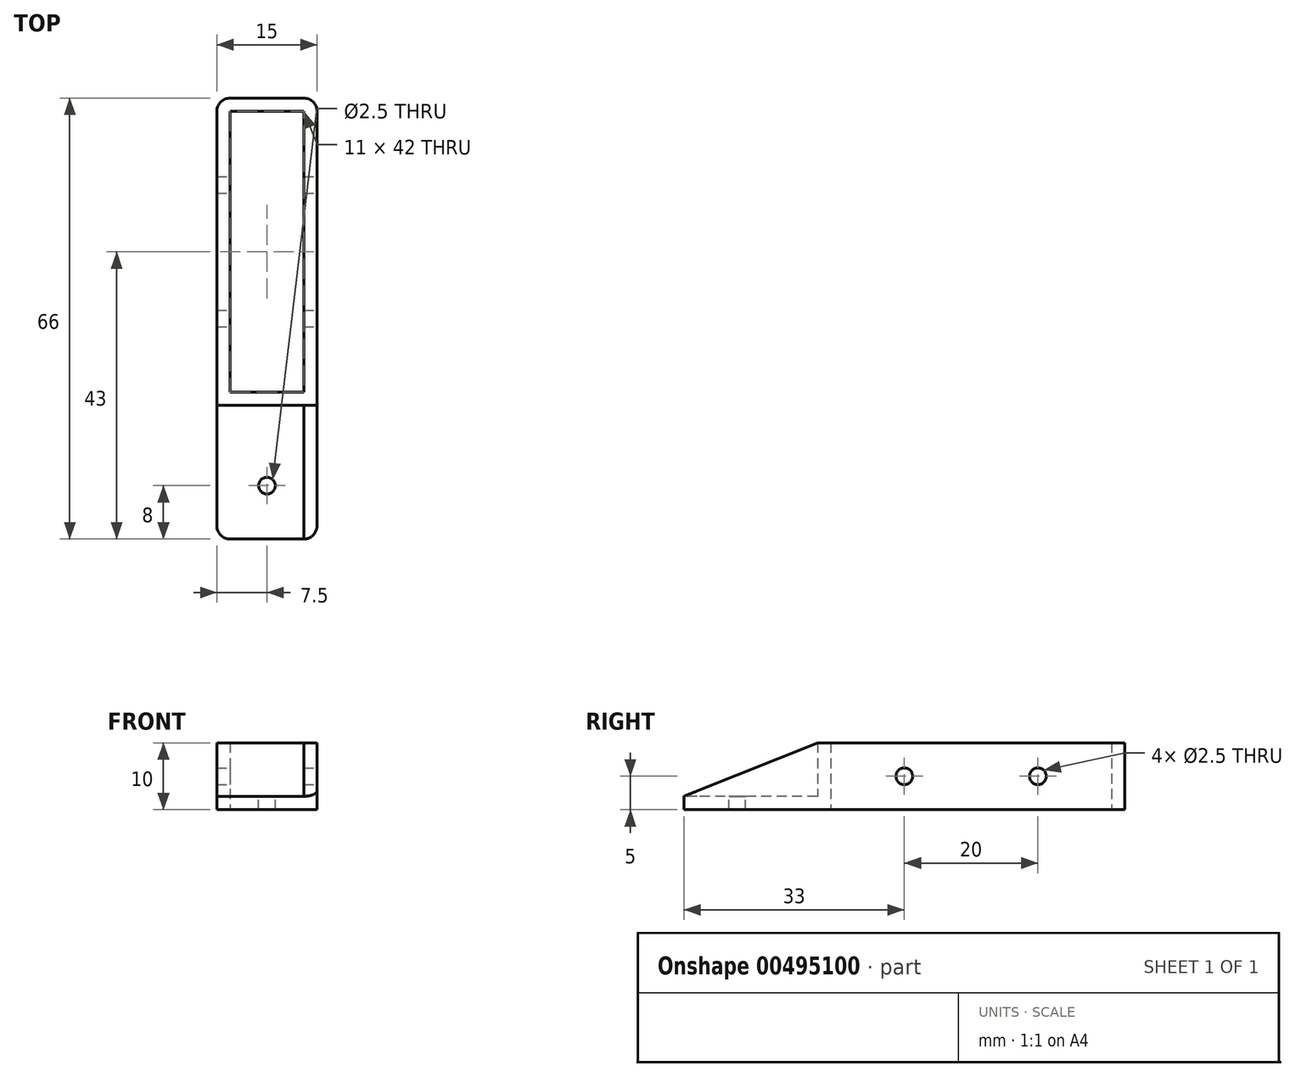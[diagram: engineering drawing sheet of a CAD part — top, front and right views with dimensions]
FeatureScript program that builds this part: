
annotation { "Feature Type Name" : "Feature", "Feature Type Description" : "" }
export const myFeature = defineFeature(function(context is Context, id is Id, definition is map)
    precondition{}
    {
        {
            var Q0;
            Q0=qCreatedBy(makeId("Top.planeOp"),FACE);
            var sketch = newSketch(context, id + "F0", { "sketchPlane" : qUnion([Q0])});
            skLineSegment(sketch, "E0.bottom", {"start": v(0, 0) * mm, "end": v(11, 0) * mm});
            skLineSegment(sketch, "E0.top", {"start": v(0, 42) * mm, "end": v(11, 42) * mm});
            skLineSegment(sketch, "E0.left", {"start": v(0, 0) * mm, "end": v(0, 42) * mm});
            skLineSegment(sketch, "E0.right", {"start": v(11, 0) * mm, "end": v(11, 42) * mm});
            skSolve(sketch);
        }
        {
            var Q0;
            Q0 = qSketchRegion(id + "F0", true);
            extrude(context, id + "F1", {"entities" : qUnion([Q0]), "depth" : 10 * mm});
        }
        {
            var Q0;
            Q0=makeQuery(id+"F1.opExtrude","CAP_FACE",FACE,{"disambiguationData":[OSD([sQuery(id+"F0.wireOp",EDGE,"E0.bottom"),sQuery(id+"F0.wireOp",EDGE,"E0.top"),sQuery(id+"F0.wireOp",EDGE,"E0.left"),sQuery(id+"F0.wireOp",EDGE,"E0.right")])],"isStart":false});
            var Q1;
            Q1=makeQuery(id+"F1.opExtrude","CAP_FACE",FACE,{"disambiguationData":[OSD([sQuery(id+"F0.wireOp",EDGE,"E0.bottom"),sQuery(id+"F0.wireOp",EDGE,"E0.top"),sQuery(id+"F0.wireOp",EDGE,"E0.left"),sQuery(id+"F0.wireOp",EDGE,"E0.right")])],"isStart":true});
            shell(context, id + "F2", {"entities" : qUnion([Q0, Q1]), "thickness" : 2 * mm, "oppositeDirection" : true});
        }
        {
            var Q0;
            Q0=qCreatedBy(makeId("Top.planeOp"),FACE);
            var sketch = newSketch(context, id + "F3", { "sketchPlane" : qUnion([Q0])});
            skLineSegment(sketch, "E1", {"start": v(-7.9, -2) * mm, "end": v(18.9, -2) * mm, "construction": true});
            skLineSegment(sketch, "E2", {"start": v(-2, 1.2) * mm, "end": v(-2, -8.45) * mm, "construction": true});
            skLineSegment(sketch, "E3", {"start": v(13, -0.65) * mm, "end": v(13, -7.97) * mm, "construction": true});
            skLineSegment(sketch, "E4.bottom", {"start": v(-2, -2) * mm, "end": v(13, -2) * mm});
            skLineSegment(sketch, "E4.top", {"start": v(-2, -22) * mm, "end": v(13, -22) * mm});
            skLineSegment(sketch, "E4.left", {"start": v(-2, -2) * mm, "end": v(-2, -22) * mm});
            skLineSegment(sketch, "E4.right", {"start": v(13, -2) * mm, "end": v(13, -22) * mm});
            skSolve(sketch);
        }
        {
            var Q0;
            Q0 = qSketchRegion(id + "F3", true);
            extrude(context, id + "F4", {"entities" : qUnion([Q0]), "operationType" : NewBodyOperationType.ADD, "depth" : 2 * mm});
        }
        {
            var Q0;
            Q0=makeQuery(id+"F4.boolean.opBoolean","MERGE",FACE,{"derivedFrom":[makeQuery(id+"F1.opExtrude","SWEPT_FACE",FACE,{"disambiguationData":[OSD([sQuery(id+"F0.wireOp",EDGE,"E0.right")])]}),makeQuery(id+"F4.opExtrude","SWEPT_FACE",FACE,{"disambiguationData":[OSD([sQuery(id+"F3.wireOp",EDGE,"E4.right")])]})]});
            var sketch = newSketch(context, id + "F5", { "sketchPlane" : qUnion([Q0])});
            skLineSegment(sketch, "E5", {"start": v(-22, 2) * mm, "end": v(-2, 10) * mm});
            skLineSegment(sketch, "E6", {"start": v(-22, 2) * mm, "end": v(-2, 2) * mm});
            skLineSegment(sketch, "E7", {"start": v(-2, 2) * mm, "end": v(-2, 10) * mm});
            skSolve(sketch);
        }
        {
            var Q0;
            Q0 = qSketchRegion(id + "F5", true);
            extrude(context, id + "F6", {"entities" : qUnion([Q0]), "operationType" : NewBodyOperationType.ADD, "oppositeDirection" : true, "depth" : 2 * mm});
        }
        {
            var Q0;
            Q0=qCreatedBy(makeId("Right.planeOp"),FACE);
            cPlane(context, id + "F7", {"entities" : qUnion([Q0]), "cplaneType" : CPlaneType.OFFSET, "offset" : 5.5 * mm, "width" : 150 * mm, "height" : 150 * mm});
        }
        {
            var Q0;
            Q0=makeQuery(id+"F4.opExtrude","CAP_FACE",FACE,{"disambiguationData":[OSD([sQuery(id+"F3.wireOp",EDGE,"E4.bottom"),sQuery(id+"F3.wireOp",EDGE,"E4.top"),sQuery(id+"F3.wireOp",EDGE,"E4.left"),sQuery(id+"F3.wireOp",EDGE,"E4.right")])],"isStart":false});
            var sketch = newSketch(context, id + "F8", { "sketchPlane" : qUnion([Q0])});
            skLineSegment(sketch, "E8", {"start": v(5.5, -2) * mm, "end": v(5.5, -23.99) * mm, "construction": true});
            skPoint(sketch, "E8.endSnap0", {"position": v(5.5, -22) * mm});
            skCircle(sketch, "E9", {"center": v(5.5, -14) * mm, "radius": 1.25 * mm});
            skSolve(sketch);
        }
        {
            var Q0;
            Q0 = qSketchRegion(id + "F8", true);
            extrude(context, id + "F9", {"entities" : qUnion([Q0]), "operationType" : NewBodyOperationType.REMOVE, "endBound" : BoundingType.THROUGH_ALL, "oppositeDirection" : true, "depth" : 25 * mm});
        }
        {
            var Q0;
            Q0=makeQuery(id+"F6.boolean.opBoolean","MERGE",FACE,{"derivedFrom":[makeQuery(id+"F4.boolean.opBoolean","MERGE",FACE,{"derivedFrom":[makeQuery(id+"F1.opExtrude","SWEPT_FACE",FACE,{"disambiguationData":[OSD([sQuery(id+"F0.wireOp",EDGE,"E0.right")])]}),makeQuery(id+"F4.opExtrude","SWEPT_FACE",FACE,{"disambiguationData":[OSD([sQuery(id+"F3.wireOp",EDGE,"E4.right")])]})]}),makeQuery(id+"F6.opExtrude","CAP_FACE",FACE,{"disambiguationData":[OSD([sQuery(id+"F5.wireOp",EDGE,"E5"),sQuery(id+"F5.wireOp",EDGE,"E6"),sQuery(id+"F5.wireOp",EDGE,"E7")])],"isStart":true})]});
            var sketch = newSketch(context, id + "F10", { "sketchPlane" : qUnion([Q0])});
            skLineSegment(sketch, "E10", {"start": v(44, 5) * mm, "end": v(-23.27, 5) * mm, "construction": true});
            skLineSegment(sketch, "E11", {"start": v(21, 10) * mm, "end": v(21, -3.03) * mm, "construction": true});
            skPoint(sketch, "E11.endSnap0", {"position": v(21, 10) * mm});
            skLineSegment(sketch, "E12", {"start": v(31, 14.53) * mm, "end": v(31, -5.73) * mm, "construction": true});
            skLineSegment(sketch, "E13", {"start": v(11, 15.6) * mm, "end": v(11, -4.52) * mm, "construction": true});
            skCircle(sketch, "E14", {"center": v(11, 5) * mm, "radius": 1.25 * mm});
            skCircle(sketch, "E15", {"center": v(31, 5) * mm, "radius": 1.25 * mm});
            skSolve(sketch);
        }
        {
            var Q0;
            Q0 = qSketchRegion(id + "F10", true);
            extrude(context, id + "F11", {"entities" : qUnion([Q0]), "operationType" : NewBodyOperationType.REMOVE, "endBound" : BoundingType.THROUGH_ALL, "oppositeDirection" : true, "depth" : 25 * mm});
        }
        {
            var Q0;
            Q0=makeQuery(id+"F1.opExtrude","SWEPT_EDGE",EDGE,{"disambiguationData":[OSD([sQuery(id+"F0.wireOp",EDGE,"E0.top"),sQuery(id+"F0.wireOp",EDGE,"E0.left")])]});
            var Q1;
            Q1=makeQuery(id+"F1.opExtrude","SWEPT_EDGE",EDGE,{"disambiguationData":[OSD([sQuery(id+"F0.wireOp",EDGE,"E0.top"),sQuery(id+"F0.wireOp",EDGE,"E0.right")])]});
            var Q2;
            Q2=makeQuery(id+"F4.opExtrude","SWEPT_EDGE",EDGE,{"disambiguationData":[OSD([sQuery(id+"F3.wireOp",EDGE,"E4.top"),sQuery(id+"F3.wireOp",EDGE,"E4.left")])]});
            var Q3;
            Q3=makeQuery(id+"F4.opExtrude","SWEPT_EDGE",EDGE,{"disambiguationData":[OSD([sQuery(id+"F3.wireOp",EDGE,"E4.top"),sQuery(id+"F3.wireOp",EDGE,"E4.right")])]});
            fillet(context, id + "F12", {"entities" : qUnion([Q0, Q1, Q2, Q3]), "radius" : 2 * mm, "tangentPropagation" : true, "allowEdgeOverflow" : false});
        }
    });
